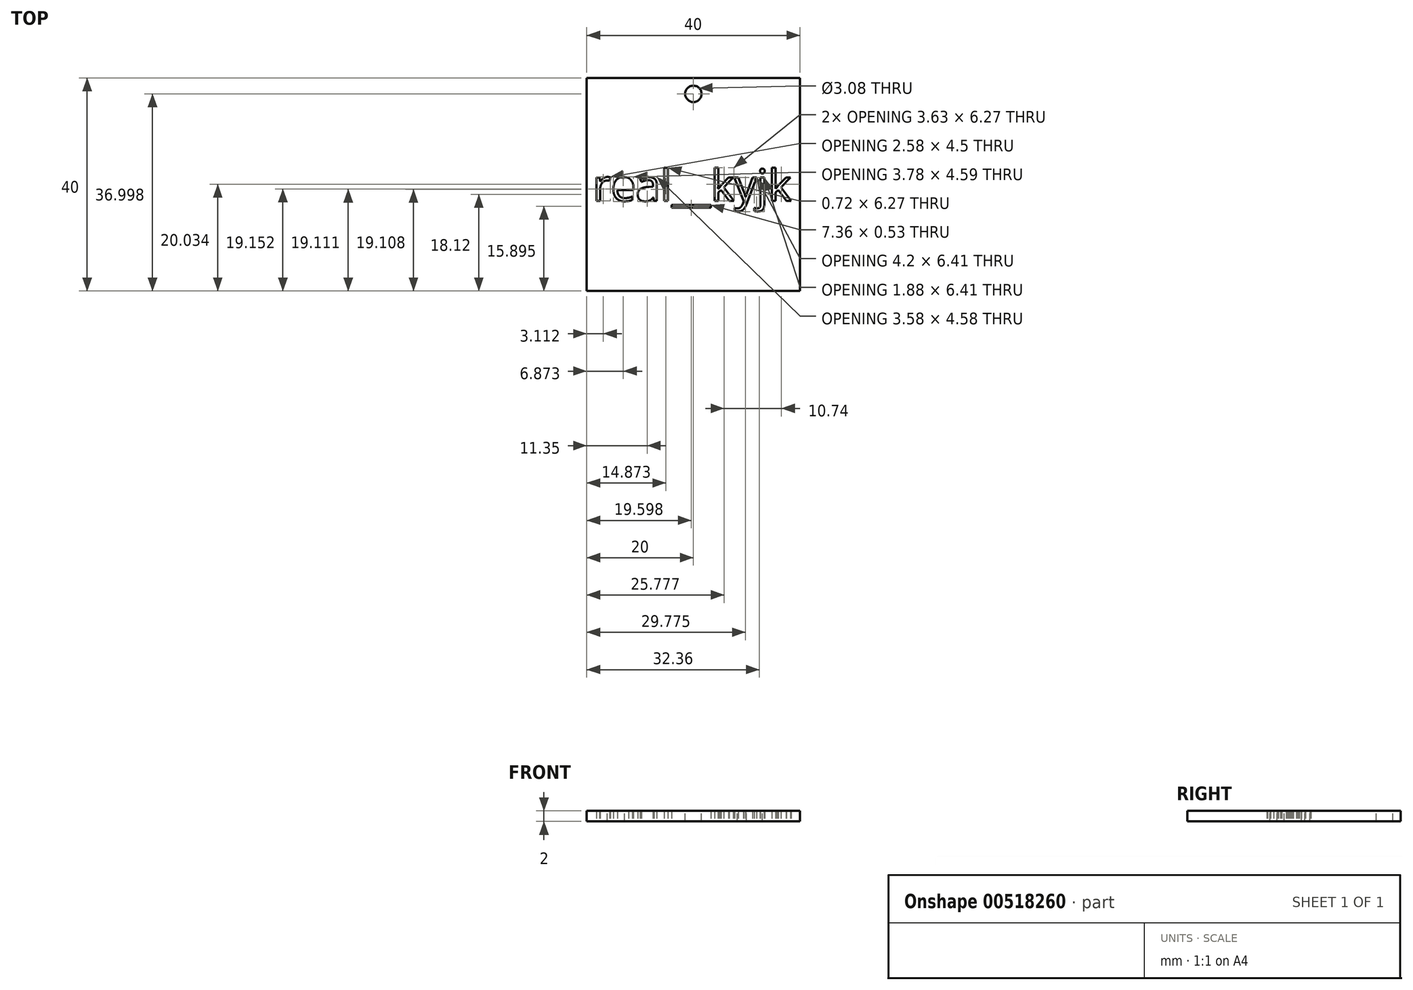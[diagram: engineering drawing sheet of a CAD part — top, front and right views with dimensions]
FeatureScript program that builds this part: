
annotation { "Feature Type Name" : "Feature", "Feature Type Description" : "" }
export const myFeature = defineFeature(function(context is Context, id is Id, definition is map)
    precondition{}
    {
        {
            var Q0;
            Q0=qCreatedBy(makeId("Top.planeOp"),FACE);
            var sketch = newSketch(context, id + "F0", { "sketchPlane" : qUnion([Q0])});
            skLineSegment(sketch, "E0.bottom", {"start": v(20, -20) * mm, "end": v(-20, -20) * mm});
            skLineSegment(sketch, "E0.top", {"start": v(20, 20) * mm, "end": v(-20, 20) * mm});
            skLineSegment(sketch, "E0.left", {"start": v(20, -20) * mm, "end": v(20, 20) * mm});
            skLineSegment(sketch, "E0.right", {"start": v(-20, -20) * mm, "end": v(-20, 20) * mm});
            skPoint(sketch, "E0.middle", {"position": v(0, 0) * mm});
            skText(sketch, "E1", { "text": "real__kyjk", "fontName": "NotoSans-Regular.ttf"});
            const initialGuessF0  = {"E1": [-0.01888, -0.0031, 1, 0, 0.00594]};
            skSetInitialGuess(sketch, initialGuessF0);
            skSolve(sketch);
        }
        {
            var Q0;
            Q0 = qSketchRegion(id + "FdGdtBfmJ0I1lv2_0", true);
            var Q1;
            Q1=makeQuery(id+"F0.imprint","IMPRINT",FACE,{"disambiguationData":[TD([[makeQuery(id+"F0.imprint","IMPRINT",EDGE,{"derivedFrom":sQuery(id+"F0.wireOp",EDGE,"E0.bottom")}),-1.0]])]});
            extrude(context, id + "F1", {"entities" : qUnion([Q0, Q1]), "depth" : 2 * mm, "offsetDistance" : 25 * mm});
        }
        {
            var Q0;
            Q0=makeQuery(id+"F1.opExtrude","CAP_FACE",FACE,{"disambiguationData":[OSD([sQuery(id+"F0.wireOp",EDGE,"E0.bottom"),sQuery(id+"F0.wireOp",EDGE,"E0.top"),sQuery(id+"F0.wireOp",EDGE,"E0.left"),sQuery(id+"F0.wireOp",EDGE,"E0.right"),sQuery(id+"F0.wireOp",EDGE,"E1.sketch_text.stroke-0"),sQuery(id+"F0.wireOp",EDGE,"E1.sketch_text.stroke-1"),sQuery(id+"F0.wireOp",EDGE,"E1.sketch_text.stroke-2"),sQuery(id+"F0.wireOp",EDGE,"E1.sketch_text.stroke-3"),sQuery(id+"F0.wireOp",EDGE,"E1.sketch_text.stroke-4"),sQuery(id+"F0.wireOp",EDGE,"E1.sketch_text.stroke-5"),sQuery(id+"F0.wireOp",EDGE,"E1.sketch_text.stroke-6"),sQuery(id+"F0.wireOp",EDGE,"E1.sketch_text.stroke-7"),sQuery(id+"F0.wireOp",EDGE,"E1.sketch_text.stroke-8"),sQuery(id+"F0.wireOp",EDGE,"E1.sketch_text.stroke-9"),sQuery(id+"F0.wireOp",EDGE,"E1.sketch_text.stroke-10"),sQuery(id+"F0.wireOp",EDGE,"E1.sketch_text.stroke-11"),sQuery(id+"F0.wireOp",EDGE,"E1.sketch_text.stroke-12"),sQuery(id+"F0.wireOp",EDGE,"E1.sketch_text.stroke-13"),sQuery(id+"F0.wireOp",EDGE,"E1.sketch_text.stroke-14"),sQuery(id+"F0.wireOp",EDGE,"E1.sketch_text.stroke-15"),sQuery(id+"F0.wireOp",EDGE,"E1.sketch_text.stroke-16"),sQuery(id+"F0.wireOp",EDGE,"E1.sketch_text.stroke-17"),sQuery(id+"F0.wireOp",EDGE,"E1.sketch_text.stroke-18"),sQuery(id+"F0.wireOp",EDGE,"E1.sketch_text.stroke-19"),sQuery(id+"F0.wireOp",EDGE,"E1.sketch_text.stroke-20"),sQuery(id+"F0.wireOp",EDGE,"E1.sketch_text.stroke-21"),sQuery(id+"F0.wireOp",EDGE,"E1.sketch_text.stroke-22"),sQuery(id+"F0.wireOp",EDGE,"E1.sketch_text.stroke-23"),sQuery(id+"F0.wireOp",EDGE,"E1.sketch_text.stroke-24"),sQuery(id+"F0.wireOp",EDGE,"E1.sketch_text.stroke-25"),sQuery(id+"F0.wireOp",EDGE,"E1.sketch_text.stroke-26"),sQuery(id+"F0.wireOp",EDGE,"E1.sketch_text.stroke-27"),sQuery(id+"F0.wireOp",EDGE,"E1.sketch_text.stroke-28"),sQuery(id+"F0.wireOp",EDGE,"E1.sketch_text.stroke-34"),sQuery(id+"F0.wireOp",EDGE,"E1.sketch_text.stroke-35"),sQuery(id+"F0.wireOp",EDGE,"E1.sketch_text.stroke-36"),sQuery(id+"F0.wireOp",EDGE,"E1.sketch_text.stroke-37"),sQuery(id+"F0.wireOp",EDGE,"E1.sketch_text.stroke-38"),sQuery(id+"F0.wireOp",EDGE,"E1.sketch_text.stroke-39"),sQuery(id+"F0.wireOp",EDGE,"E1.sketch_text.stroke-40"),sQuery(id+"F0.wireOp",EDGE,"E1.sketch_text.stroke-41"),sQuery(id+"F0.wireOp",EDGE,"E1.sketch_text.stroke-42"),sQuery(id+"F0.wireOp",EDGE,"E1.sketch_text.stroke-43"),sQuery(id+"F0.wireOp",EDGE,"E1.sketch_text.stroke-44"),sQuery(id+"F0.wireOp",EDGE,"E1.sketch_text.stroke-45"),sQuery(id+"F0.wireOp",EDGE,"E1.sketch_text.stroke-46"),sQuery(id+"F0.wireOp",EDGE,"E1.sketch_text.stroke-47"),sQuery(id+"F0.wireOp",EDGE,"E1.sketch_text.stroke-48"),sQuery(id+"F0.wireOp",EDGE,"E1.sketch_text.stroke-49"),sQuery(id+"F0.wireOp",EDGE,"E1.sketch_text.stroke-50"),sQuery(id+"F0.wireOp",EDGE,"E1.sketch_text.stroke-51"),sQuery(id+"F0.wireOp",EDGE,"E1.sketch_text.stroke-52"),sQuery(id+"F0.wireOp",EDGE,"E1.sketch_text.stroke-53"),sQuery(id+"F0.wireOp",EDGE,"E1.sketch_text.stroke-62"),sQuery(id+"F0.wireOp",EDGE,"E1.sketch_text.stroke-63"),sQuery(id+"F0.wireOp",EDGE,"E1.sketch_text.stroke-64"),sQuery(id+"F0.wireOp",EDGE,"E1.sketch_text.stroke-65"),sQuery(id+"F0.wireOp",EDGE,"E1.sketch_text.stroke-66"),sQuery(id+"F0.wireOp",EDGE,"E1.sketch_text.stroke-67"),sQuery(id+"F0.wireOp",EDGE,"E1.sketch_text.stroke-68"),sQuery(id+"F0.wireOp",EDGE,"E1.sketch_text.stroke-70"),sQuery(id+"F0.wireOp",EDGE,"E1.sketch_text.stroke-72"),sQuery(id+"F0.wireOp",EDGE,"E1.sketch_text.stroke-73"),sQuery(id+"F0.wireOp",EDGE,"E1.sketch_text.stroke-74"),sQuery(id+"F0.wireOp",EDGE,"E1.sketch_text.stroke-75"),sQuery(id+"F0.wireOp",EDGE,"E1.sketch_text.stroke-76"),sQuery(id+"F0.wireOp",EDGE,"E1.sketch_text.stroke-77"),sQuery(id+"F0.wireOp",EDGE,"E1.sketch_text.stroke-78"),sQuery(id+"F0.wireOp",EDGE,"E1.sketch_text.stroke-79"),sQuery(id+"F0.wireOp",EDGE,"E1.sketch_text.stroke-80"),sQuery(id+"F0.wireOp",EDGE,"E1.sketch_text.stroke-81"),sQuery(id+"F0.wireOp",EDGE,"E1.sketch_text.stroke-82"),sQuery(id+"F0.wireOp",EDGE,"E1.sketch_text.stroke-83"),sQuery(id+"F0.wireOp",EDGE,"E1.sketch_text.stroke-84"),sQuery(id+"F0.wireOp",EDGE,"E1.sketch_text.stroke-85"),sQuery(id+"F0.wireOp",EDGE,"E1.sketch_text.stroke-86"),sQuery(id+"F0.wireOp",EDGE,"E1.sketch_text.stroke-87"),sQuery(id+"F0.wireOp",EDGE,"E1.sketch_text.stroke-88"),sQuery(id+"F0.wireOp",EDGE,"E1.sketch_text.stroke-89"),sQuery(id+"F0.wireOp",EDGE,"E1.sketch_text.stroke-90"),sQuery(id+"F0.wireOp",EDGE,"E1.sketch_text.stroke-91"),sQuery(id+"F0.wireOp",EDGE,"E1.sketch_text.stroke-92"),sQuery(id+"F0.wireOp",EDGE,"E1.sketch_text.stroke-93"),sQuery(id+"F0.wireOp",EDGE,"E1.sketch_text.stroke-94"),sQuery(id+"F0.wireOp",EDGE,"E1.sketch_text.stroke-95"),sQuery(id+"F0.wireOp",EDGE,"E1.sketch_text.stroke-96"),sQuery(id+"F0.wireOp",EDGE,"E1.sketch_text.stroke-97"),sQuery(id+"F0.wireOp",EDGE,"E1.sketch_text.stroke-98"),sQuery(id+"F0.wireOp",EDGE,"E1.sketch_text.stroke-99"),sQuery(id+"F0.wireOp",EDGE,"E1.sketch_text.stroke-100"),sQuery(id+"F0.wireOp",EDGE,"E1.sketch_text.stroke-101"),sQuery(id+"F0.wireOp",EDGE,"E1.sketch_text.stroke-102"),sQuery(id+"F0.wireOp",EDGE,"E1.sketch_text.stroke-103"),sQuery(id+"F0.wireOp",EDGE,"E1.sketch_text.stroke-104"),sQuery(id+"F0.wireOp",EDGE,"E1.sketch_text.stroke-105"),sQuery(id+"F0.wireOp",EDGE,"E1.sketch_text.stroke-106"),sQuery(id+"F0.wireOp",EDGE,"E1.sketch_text.stroke-107"),sQuery(id+"F0.wireOp",EDGE,"E1.sketch_text.stroke-108"),sQuery(id+"F0.wireOp",EDGE,"E1.sketch_text.stroke-109"),sQuery(id+"F0.wireOp",EDGE,"E1.sketch_text.stroke-110"),sQuery(id+"F0.wireOp",EDGE,"E1.sketch_text.stroke-111"),sQuery(id+"F0.wireOp",EDGE,"E1.sketch_text.stroke-112"),sQuery(id+"F0.wireOp",EDGE,"E1.sketch_text.stroke-113"),sQuery(id+"F0.wireOp",EDGE,"E1.sketch_text.stroke-114"),sQuery(id+"F0.wireOp",EDGE,"E1.sketch_text.stroke-115"),sQuery(id+"F0.wireOp",EDGE,"E1.sketch_text.stroke-116"),sQuery(id+"F0.wireOp",EDGE,"E1.sketch_text.stroke-117"),sQuery(id+"F0.wireOp",EDGE,"E1.sketch_text.stroke-118"),sQuery(id+"F0.wireOp",EDGE,"E1.sketch_text.stroke-119"),sQuery(id+"F0.wireOp",EDGE,"E1.sketch_text.stroke-120"),sQuery(id+"F0.wireOp",EDGE,"E1.sketch_text.stroke-121"),sQuery(id+"F0.wireOp",EDGE,"E1.sketch_text.stroke-122"),sQuery(id+"F0.wireOp",EDGE,"E1.sketch_text.stroke-123"),sQuery(id+"F0.wireOp",EDGE,"E1.sketch_text.stroke-124"),sQuery(id+"F0.wireOp",EDGE,"E1.sketch_text.stroke-125"),sQuery(id+"F0.wireOp",EDGE,"E1.sketch_text.stroke-126"),sQuery(id+"F0.wireOp",EDGE,"E1.sketch_text.stroke-127"),sQuery(id+"F0.wireOp",EDGE,"E1.sketch_text.stroke-128"),sQuery(id+"F0.wireOp",EDGE,"E1.sketch_text.stroke-129"),sQuery(id+"F0.wireOp",EDGE,"E1.sketch_text.stroke-130"),sQuery(id+"F0.wireOp",EDGE,"E1.sketch_text.stroke-131"),sQuery(id+"F0.wireOp",EDGE,"E1.sketch_text.stroke-132"),sQuery(id+"F0.wireOp",EDGE,"E1.sketch_text.stroke-133"),sQuery(id+"F0.wireOp",EDGE,"E1.sketch_text.stroke-134"),sQuery(id+"F0.wireOp",EDGE,"E1.sketch_text.stroke-135"),sQuery(id+"F0.wireOp",EDGE,"E1.sketch_text.stroke-136"),sQuery(id+"F0.wireOp",EDGE,"E1.sketch_text.stroke-137"),sQuery(id+"F0.wireOp",EDGE,"E1.sketch_text.stroke-138"),sQuery(id+"F0.wireOp",EDGE,"E1.sketch_text.stroke-139"),sQuery(id+"F0.wireOp",EDGE,"E1.sketch_text.stroke-140"),sQuery(id+"F0.wireOp",EDGE,"E1.sketch_text.stroke-141")])],"isStart":false});
            var sketch = newSketch(context, id + "F2", { "sketchPlane" : qUnion([Q0])});
            skCircle(sketch, "E2", {"center": v(0, 17) * mm, "radius": 1.54 * mm});
            skSolve(sketch);
        }
        {
            var Q0;
            Q0=makeQuery(id+"F2.imprint","IMPRINT",FACE,{"disambiguationData":[TD([[makeQuery(id+"F2.imprint","IMPRINT",EDGE,{"derivedFrom":sQuery(id+"F2.wireOp",EDGE,"E2")}),1.0]])]});
            extrude(context, id + "F3", {"entities" : qUnion([Q0]), "operationType" : NewBodyOperationType.REMOVE, "oppositeDirection" : true, "depth" : 2 * mm, "offsetDistance" : 25 * mm});
        }
    });
